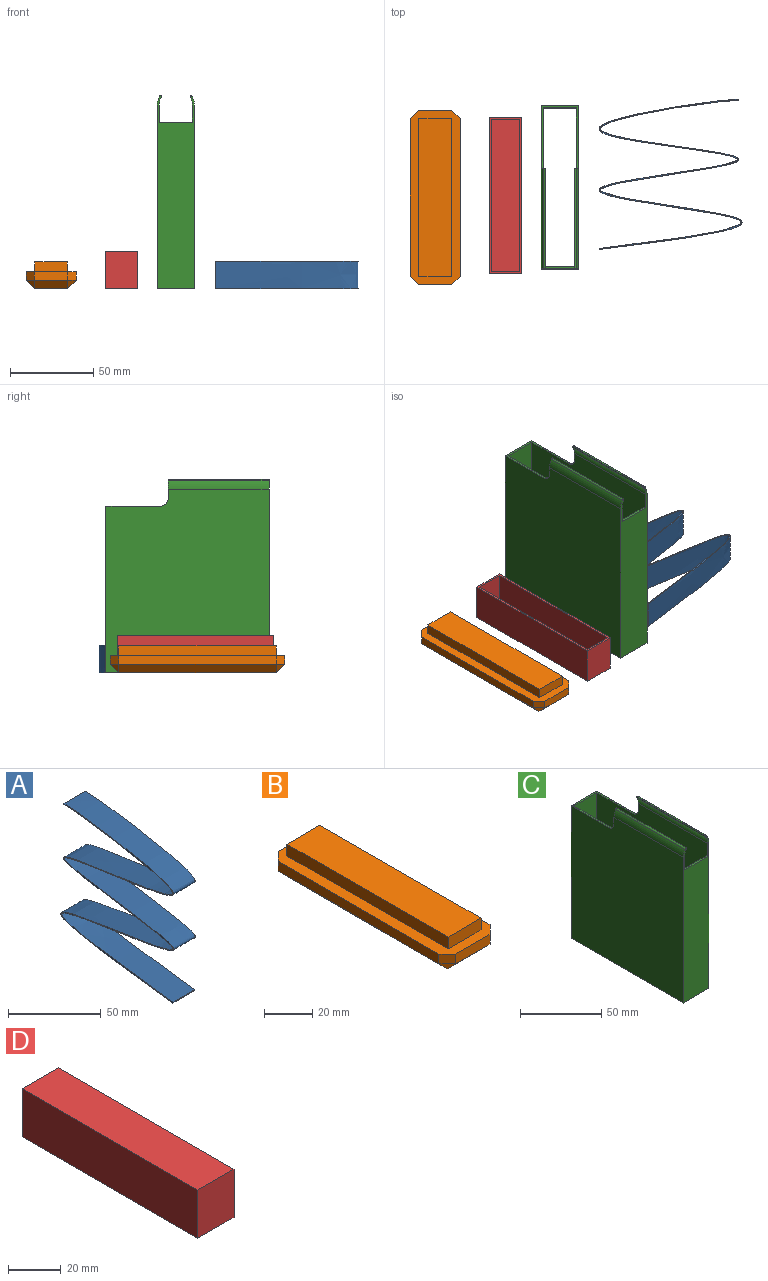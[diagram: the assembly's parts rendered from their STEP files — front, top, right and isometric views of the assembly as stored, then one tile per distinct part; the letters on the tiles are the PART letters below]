
ASSEMBLY  parts=4 mates=3
PART A: 6 faces, bbox 16.5x85.9x90.2 mm
  f0: plane 90.21x85.93mm, normal (-1,0,0), area 316mm2, adj f1,f3,f4,f5
  f1: plane 16.5x0.61mm, normal (0,-0.99,-0.12), area 10.1mm2, adj f0,f2,f4,f5
  f2: plane 90.21x85.93mm, normal (1,0,0), area 316mm2, adj f1,f3,f4,f5
  f3: plane 16.5x0.61mm, normal (0,1,0), area 10.1mm2, adj f0,f2,f4,f5
  f4: extruded ~89.61x84.6mm, area 7319.4mm2, adj f0,f1,f2,f3
  f5: extruded ~89.6x84.98mm, area 7313.1mm2, adj f0,f1,f2,f3
PART B: 23 faces, bbox 30.1x104.8x16 mm
  f0: plane 19.4x6mm, normal (0,-1,0), area 116.4mm2, adj f1,f3,f4,f10
  f1: plane 94.9x6mm, normal (-1,0,0), area 569.4mm2, adj f0,f2,f4,f10
  f2: plane 19.4x6mm, normal (0,1,0), area 116.4mm2, adj f1,f3,f4,f10
  f3: plane 94.9x6mm, normal (1,0,0), area 569.4mm2, adj f0,f2,f4,f10
  f4: plane 94.9x19.4mm, normal (0,0,1), area 1841.1mm2, adj f0,f1,f2,f3
  f5: plane 94.77x5mm, normal (-1,0,0), area 473.8mm2, adj f10,f11,f15,f16
  f6: plane 20.13x5mm, normal (0,1,0), area 100.6mm2, adj f10,f11,f13,f14
  f7: plane 94.77x5mm, normal (1,0,0), area 473.8mm2, adj f10,f13,f19,f22
  f8: plane 20.13x5mm, normal (0,-1,0), area 100.6mm2, adj f10,f16,f20,f22
  f9: plane 94.77x20.13mm, normal (0,0,-1), area 1907.4mm2, adj f14,f15,f19,f20
  f10: plane 104.77x30.13mm, normal (0,0,1), area 1265.3mm2, adj f0,f1,f2,f3,f5,f6,f7,f8
  f11: plane 5x5mm, normal (-0.71,0.71,0), area 35.4mm2, adj f5,f6,f10,f12
  f12: plane 5x5mm, normal (-0.58,0.58,-0.58), area 21.7mm2, adj f11,f14,f15
  f13: plane 5x5mm, normal (0.71,0.71,0), area 35.4mm2, adj f6,f7,f10,f17
  f14: plane 20.13x5mm, normal (0,0.71,-0.71), area 142.3mm2, adj f6,f9,f12,f17
  f15: plane 94.77x5mm, normal (-0.71,0,-0.71), area 670.1mm2, adj f5,f9,f12,f18
  f16: plane 5x5mm, normal (-0.71,-0.71,0), area 35.4mm2, adj f5,f8,f10,f18
  f17: plane 5x5mm, normal (0.58,0.58,-0.58), area 21.7mm2, adj f13,f14,f19
  f18: plane 5x5mm, normal (-0.58,-0.58,-0.58), area 21.7mm2, adj f15,f16,f20
  f19: plane 94.77x5mm, normal (0.71,0,-0.71), area 670.1mm2, adj f7,f9,f17,f21
  f20: plane 20.13x5mm, normal (0,-0.71,-0.71), area 142.3mm2, adj f8,f9,f18,f21
  f21: plane 5x5mm, normal (0.58,-0.58,-0.58), area 21.7mm2, adj f19,f20,f22
  f22: plane 5x5mm, normal (0.71,-0.71,0), area 35.4mm2, adj f7,f8,f10,f21
PART C: 23 faces, bbox 22.4x98x116 mm
  f0: plane 32.5x22.4mm, normal (0,0,1), area 103mm2, adj f3,f5,f6,f7,f8,f9,f21,f22
  f1: plane 20x1.25mm, normal (0,0,1), area 25mm2, adj f4,f7,f9,f10
  f2: plane 98x22.4mm, normal (0,0,-1), area 285.2mm2, adj f3,f4,f5,f6,f7,f8,f9,f10
  f3: plane 100x22.4mm, normal (0,1,0), area 2240mm2, adj f0,f2,f5,f6
  f4: plane 116x22.4mm, normal (0,-1,0), area 2278.7mm2, adj f1,f2,f5,f6,f7,f9,f11,f12
  f5: plane 110x98mm, normal (1,0,0), area 10410.4mm2, adj f0,f2,f3,f4,f12,f13,f21
  f6: plane 110x98mm, normal (-1,0,0), area 10410.4mm2, adj f0,f2,f3,f4,f15,f16,f22
  f7: plane 110x96.75mm, normal (1,0,0), area 10160.4mm2, adj f0,f1,f2,f4,f8,f10,f14,f16
  f8: plane 100x20mm, normal (0,-1,0), area 2000mm2, adj f0,f2,f7,f9
  f9: plane 110x96.75mm, normal (-1,0,0), area 10160.4mm2, adj f0,f1,f2,f4,f8,f10,f11,f13
  f10: plane 100x20mm, normal (0,1,0), area 2000mm2, adj f1,f2,f7,f9
  f11: cylinder r=10mm len=60.5mm, axis (0,-1,0), area 314.5mm2, adj f4,f9,f13,f17
  f12: cylinder r=11.2mm len=60.5mm, axis (0,-1,0), area 347.4mm2, adj f4,f5,f13,f18
  f13: plane 11x2.65mm, normal (0,1,0), area 13.4mm2, adj f5,f9,f11,f12,f17,f18,f21
  f14: cylinder r=10mm len=60.5mm, axis (0,-1,0), area 314.5mm2, adj f4,f7,f16,f19
  f15: cylinder r=11.2mm len=60.5mm, axis (0,-1,0), area 347.4mm2, adj f4,f6,f16,f20
  f16: plane 11x2.65mm, normal (0,1,0), area 13.4mm2, adj f6,f7,f14,f15,f19,f20,f22
  f17: cylinder r=1mm len=60.5mm, axis (0,-1,0), area 64.5mm2, adj f4,f11,f13,f18
  f18: cylinder r=1mm len=60.5mm, axis (0,-1,0), area 76mm2, adj f4,f12,f13,f17
  f19: cylinder r=1mm len=60.5mm, axis (0,-1,0), area 64.5mm2, adj f4,f14,f16,f20
  f20: cylinder r=1mm len=60.5mm, axis (0,-1,0), area 76mm2, adj f4,f15,f16,f19
  f21: cylinder r=5mm len=5mm, axis (1,0,0), area 9.4mm2, adj f0,f5,f9,f13
  f22: cylinder r=5mm len=5mm, axis (1,0,0), area 9.4mm2, adj f0,f6,f7,f16
PART D: 11 faces, bbox 19.4x94.1x22.3 mm
  f0: plane 94.09x19.4mm, normal (0,0,-1), area 266.6mm2, adj f1,f3,f4,f5,f6,f8,f9,f10
  f1: plane 22.29x19.4mm, normal (0,-1,0), area 432.4mm2, adj f0,f2,f4,f5
  f2: plane 94.09x19.4mm, normal (0,0,1), area 1825.4mm2, adj f1,f3,f4,f5
  f3: plane 22.29x19.4mm, normal (0,1,0), area 432.4mm2, adj f0,f2,f4,f5
  f4: plane 94.09x22.29mm, normal (-1,0,0), area 2097.4mm2, adj f0,f1,f2,f3
  f5: plane 94.09x22.29mm, normal (1,0,0), area 2097.4mm2, adj f0,f1,f2,f3
  f6: plane 21.09x17mm, normal (0,1,0), area 358.5mm2, adj f0,f7,f9,f10
  f7: plane 91.69x17mm, normal (0,0,-1), area 1558.7mm2, adj f6,f8,f9,f10
  f8: plane 21.09x17mm, normal (0,-1,0), area 358.5mm2, adj f0,f7,f9,f10
  f9: plane 91.69x21.09mm, normal (1,0,0), area 1933.8mm2, adj f0,f6,f7,f8
  f10: plane 91.69x21.09mm, normal (-1,0,0), area 1933.8mm2, adj f0,f6,f7,f8
PLACE A rot(axis=(-0.58,-0.58,-0.58),120deg) t=(77.94,9.19,-38.44)mm
PLACE B t=(-74.97,-6,43.96)mm
PLACE C t=(0,0,33.96)mm fixed
PLACE D rot(axis=(-1,0,0),180deg) t=(-11.62,-4.73,31.88)mm
MATE planar B.f9 <-> C.f2  axis (0,0,-1) through (-63.77,-6,-16.04)mm
MATE planar A.f0 <-> C.f2  axis (0,0,-1) through (76.99,7.38,-16.04)mm
MATE planar D.f2 <-> C.f2  axis (0,0,-1) through (-21.32,-4.73,-16.04)mm
